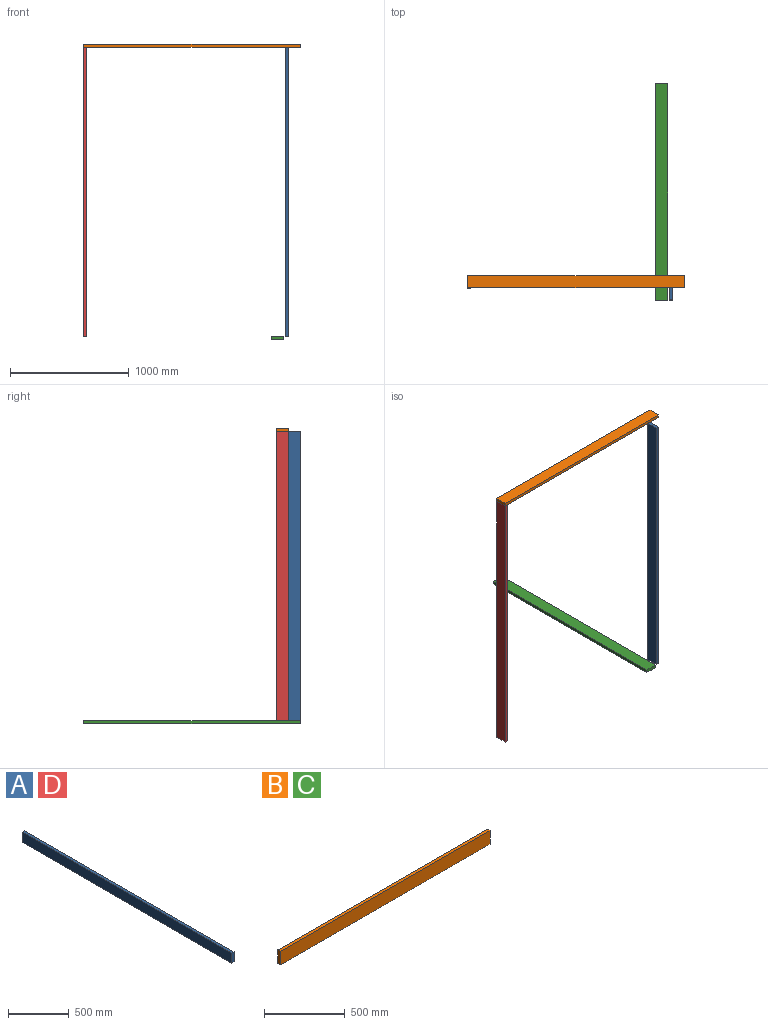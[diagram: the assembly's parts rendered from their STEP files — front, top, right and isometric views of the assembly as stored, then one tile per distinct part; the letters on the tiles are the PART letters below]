
ASSEMBLY  parts=4 mates=6
PART A: 6 faces, bbox 25.4x2438.4x101.6 mm
  f0: plane 2438.4x25.4mm, normal (0,0,1), area 61935.4mm2, adj f1,f3,f4,f5
  f1: plane 101.6x25.4mm, normal (0,-1,0), area 2580.6mm2, adj f0,f2,f4,f5
  f2: plane 2438.4x25.4mm, normal (0,0,-1), area 61935.4mm2, adj f1,f3,f4,f5
  f3: plane 101.6x25.4mm, normal (0,1,0), area 2580.6mm2, adj f0,f2,f4,f5
  f4: plane 2438.4x101.6mm, normal (1,0,0), area 247741.4mm2, adj f0,f1,f2,f3
  f5: plane 2438.4x101.6mm, normal (-1,0,0), area 247741.4mm2, adj f0,f1,f2,f3
PART B: 6 faces, bbox 1828.8x25.4x101.6 mm
  f0: plane 1828.8x25.4mm, normal (0,0,1), area 46451.5mm2, adj f1,f3,f4,f5
  f1: plane 101.6x25.4mm, normal (-1,0,0), area 2580.6mm2, adj f0,f2,f4,f5
  f2: plane 1828.8x25.4mm, normal (0,0,-1), area 46451.5mm2, adj f1,f3,f4,f5
  f3: plane 101.6x25.4mm, normal (1,0,0), area 2580.6mm2, adj f0,f2,f4,f5
  f4: plane 1828.8x101.6mm, normal (0,-1,0), area 185806.1mm2, adj f0,f1,f2,f3
  f5: plane 1828.8x101.6mm, normal (0,1,0), area 185806.1mm2, adj f0,f1,f2,f3
PART C: same geometry as B
PART D: same geometry as A
PLACE A rot(axis=(1,0,0),90deg) t=(1286.43,490.89,1451.36)mm
PLACE B rot(axis=(1,0,0),90deg) t=(499.03,592.49,2695.96)mm
PLACE C rot(axis=(0.58,-0.58,-0.58),120deg) t=(1223.84,1354.49,232.16)mm
PLACE D rot(axis=(1,0,0),90deg) t=(-415.37,592.49,1451.36)mm
MATE planar C.f5 <-> A.f1  axis (0,0,1) through (1223.84,440.09,232.16)mm
MATE planar D.f3 <-> B.f4  axis (0,0,1) through (-402.67,592.49,2670.56)mm
MATE planar A.f0 <-> C.f3  axis (0,-1,0) through (1286.43,440.09,232.16)mm
MATE planar B.f0 <-> A.f2  axis (0,-1,0) through (499.03,541.69,2683.26)mm
MATE planar D.f5 <-> B.f1  axis (-1,0,0) through (-415.37,592.49,2670.56)mm
MATE planar B.f0 <-> D.f0  axis (0,-1,0) through (499.03,541.69,2683.26)mm
